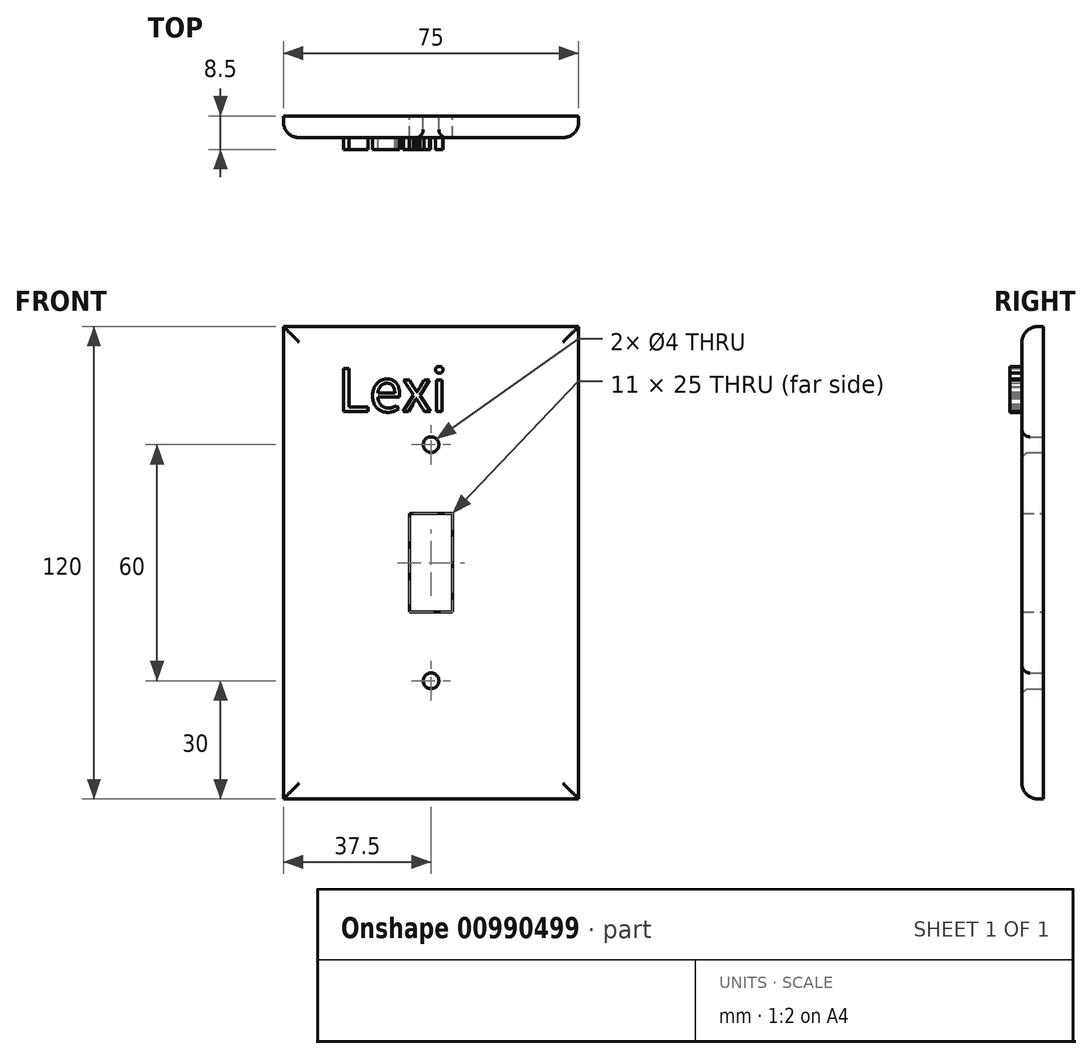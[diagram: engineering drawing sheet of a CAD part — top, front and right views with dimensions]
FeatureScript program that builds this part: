
annotation { "Feature Type Name" : "Feature", "Feature Type Description" : "" }
export const myFeature = defineFeature(function(context is Context, id is Id, definition is map)
    precondition{}
    {
        {
            var Q0;
            Q0=qCreatedBy(makeId("Front.planeOp"),FACE);
            var sketch = newSketch(context, id + "F0", { "sketchPlane" : qUnion([Q0])});
            skLineSegment(sketch, "E0.bottom", {"start": v(37.5, 60) * mm, "end": v(-37.5, 60) * mm});
            skLineSegment(sketch, "E0.top", {"start": v(37.5, -60) * mm, "end": v(-37.5, -60) * mm});
            skLineSegment(sketch, "E0.left", {"start": v(37.5, 60) * mm, "end": v(37.5, -60) * mm});
            skLineSegment(sketch, "E0.right", {"start": v(-37.5, 60) * mm, "end": v(-37.5, -60) * mm});
            skPoint(sketch, "E0.middle", {"position": v(0, 0) * mm});
            skLineSegment(sketch, "E1.bottom", {"start": v(5.5, 12.5) * mm, "end": v(-5.5, 12.5) * mm});
            skLineSegment(sketch, "E1.top", {"start": v(5.5, -12.5) * mm, "end": v(-5.5, -12.5) * mm});
            skLineSegment(sketch, "E1.left", {"start": v(5.5, 12.5) * mm, "end": v(5.5, -12.5) * mm});
            skLineSegment(sketch, "E1.right", {"start": v(-5.5, 12.5) * mm, "end": v(-5.5, -12.5) * mm});
            skCircle(sketch, "E2", {"center": v(0, -30) * mm, "radius": 2 * mm});
            skPoint(sketch, "E3.centerSnap0", {"position": v(0, -12.5) * mm});
            skCircle(sketch, "E4", {"center": v(0, 30) * mm, "radius": 2 * mm});
            skSolve(sketch);
        }
        {
            var Q0;
            Q0=qSketchRegion(id+"F0",true);
            extrude(context, id + "F1", {"entities" : qUnion([Q0]), "depth" : 5.5 * mm, "offsetDistance" : 25 * mm});
        }
        {
            var Q0;
            Q0=makeQuery(id+"F1.opExtrude","CAP_EDGE",EDGE,{"disambiguationData":[OSD([sQuery(id+"F0.wireOp",EDGE,"E0.right")])],"isStart":false});
            var Q1;
            Q1=makeQuery(id+"F1.opExtrude","CAP_EDGE",EDGE,{"disambiguationData":[OSD([sQuery(id+"F0.wireOp",EDGE,"E0.bottom")])],"isStart":false});
            var Q2;
            Q2=makeQuery(id+"F1.opExtrude","CAP_EDGE",EDGE,{"disambiguationData":[OSD([sQuery(id+"F0.wireOp",EDGE,"E0.left")])],"isStart":false});
            var Q3;
            Q3=makeQuery(id+"F1.opExtrude","CAP_EDGE",EDGE,{"disambiguationData":[OSD([sQuery(id+"F0.wireOp",EDGE,"E0.top")])],"isStart":false});
            fillet(context, id + "F2", {"entities" : qUnion([Q0, Q1, Q2, Q3]), "radius" : 4 * mm, "tangentPropagation" : true, "allowEdgeOverflow" : false});
        }
        {
            var Q0;
            Q0=makeQuery(id+"F1.opExtrude","CAP_EDGE",EDGE,{"disambiguationData":[OSD([sQuery(id+"F0.wireOp",EDGE,"E4")])],"isStart":false});
            var Q1;
            Q1=makeQuery(id+"F1.opExtrude","CAP_EDGE",EDGE,{"disambiguationData":[OSD([sQuery(id+"F0.wireOp",EDGE,"E2")])],"isStart":false});
            fillet(context, id + "F3", {"entities" : qUnion([Q0, Q1]), "radius" : 2 * mm, "tangentPropagation" : true, "allowEdgeOverflow" : false});
        }
        {
            var Q0;
            Q0=makeQuery(id+"F1.opExtrude","CAP_FACE",FACE,{"disambiguationData":[OSD([sQuery(id+"F0.wireOp",EDGE,"E0.bottom"),sQuery(id+"F0.wireOp",EDGE,"E0.top"),sQuery(id+"F0.wireOp",EDGE,"E0.left"),sQuery(id+"F0.wireOp",EDGE,"E0.right"),sQuery(id+"F0.wireOp",EDGE,"E1.bottom"),sQuery(id+"F0.wireOp",EDGE,"E1.top"),sQuery(id+"F0.wireOp",EDGE,"E1.left"),sQuery(id+"F0.wireOp",EDGE,"E1.right"),sQuery(id+"F0.wireOp",EDGE,"E2"),sQuery(id+"F0.wireOp",EDGE,"E4")])],"isStart":false});
            var sketch = newSketch(context, id + "F4", { "sketchPlane" : qUnion([Q0])});
            skText(sketch, "E5", { "text": "Lexi", "fontName": "NotoSansCJKtc-Regular.otf"});
            const initialGuessF4  = {"E5": [-0.0237, 0.0384, 1, 0, 0.01072]};
            skSetInitialGuess(sketch, initialGuessF4);
            skSolve(sketch);
        }
        {
            var Q0;
            Q0 = qSketchRegion(id + "F4", true);
            extrude(context, id + "F5", {"entities" : qUnion([Q0]), "operationType" : NewBodyOperationType.ADD, "depth" : 3 * mm, "offsetDistance" : 25 * mm});
        }
    });
